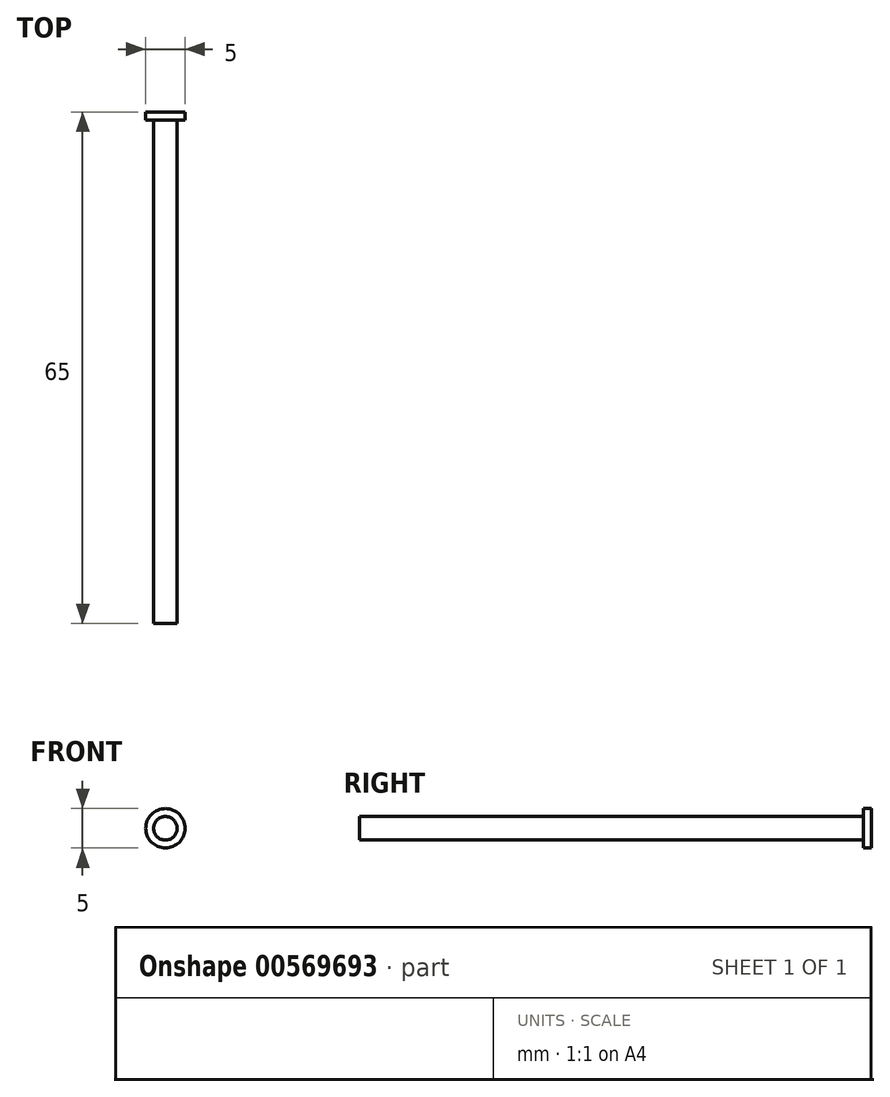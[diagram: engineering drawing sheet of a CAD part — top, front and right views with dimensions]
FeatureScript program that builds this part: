
annotation { "Feature Type Name" : "Feature", "Feature Type Description" : "" }
export const myFeature = defineFeature(function(context is Context, id is Id, definition is map)
    precondition{}
    {
        {
            var Q0;
            Q0=qCreatedBy(makeId("Front.planeOp"),FACE);
            var sketch = newSketch(context, id + "F0", { "sketchPlane" : qUnion([Q0])});
            skCircle(sketch, "E0", {"center": v(0, 0) * mm, "radius": 2.5 * mm});
            skCircle(sketch, "E1", {"center": v(0, 0) * mm, "radius": 1.5 * mm});
            skSolve(sketch);
        }
        {
            var Q0;
            Q0 = qSketchRegion(id + "F0", true);
            var Q1;
            Q1=makeQuery(id+"F0.imprint","IMPRINT",FACE,{"disambiguationData":[TD([[makeQuery(id+"F0.imprint","IMPRINT",EDGE,{"derivedFrom":sQuery(id+"F0.wireOp",EDGE,"E1")}),1.0]])]});
            extrude(context, id + "F1", {"entities" : qUnion([Q0, Q1]), "depth" : 1 * mm, "offsetDistance" : 25 * mm});
        }
        {
            var Q0;
            Q0=makeQuery(id+"F0.imprint","IMPRINT",FACE,{"disambiguationData":[TD([[makeQuery(id+"F0.imprint","IMPRINT",EDGE,{"derivedFrom":sQuery(id+"F0.wireOp",EDGE,"E1")}),1.0]])]});
            extrude(context, id + "F2", {"entities" : qUnion([Q0]), "operationType" : NewBodyOperationType.ADD, "depth" : 64 * mm, "offsetDistance" : 25 * mm});
        }
        {
            var Q0;
            Q0=makeQuery(id+"F2.opExtrude","CAP_FACE",FACE,{"disambiguationData":[OSD([sQuery(id+"F0.wireOp",EDGE,"E1")])],"isStart":false});
            extrude(context, id + "F3", {"entities" : qUnion([Q0]), "operationType" : NewBodyOperationType.ADD, "depth" : 1 * mm, "offsetDistance" : 25 * mm});
        }
    });
